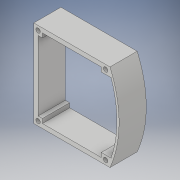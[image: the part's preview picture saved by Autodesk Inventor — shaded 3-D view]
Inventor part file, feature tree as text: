
AUTODESK INVENTOR PART (.ipt)
format: ipt  version: 2018 (Build 220112000, 112)  size: 130,048 bytes
history: native  units: in
note: dims shown in document units (in); Inventor stores cm internally (conversion verified against a paired STEP export)
features: extrude x1, sketch x1
ambient origin geometry x8: Origin, YZ Plane, XZ Plane, XY Plane, X Axis, Y Axis, Z Axis, Center Point
bodies: Solid1 (feature_tree)
feature tree (2):
  extrude  "Extrusion1"  Depth=1.248in
  sketch  "Sketch1"  dims[d0=4.0in d1=3.5in d2=3.5in d3=5.0in d4=0.2in d5=0.2in d6=0.2031in d7=0.4in d8=0.4in d9=0.1in d10=1.248in d11=0.0in]
